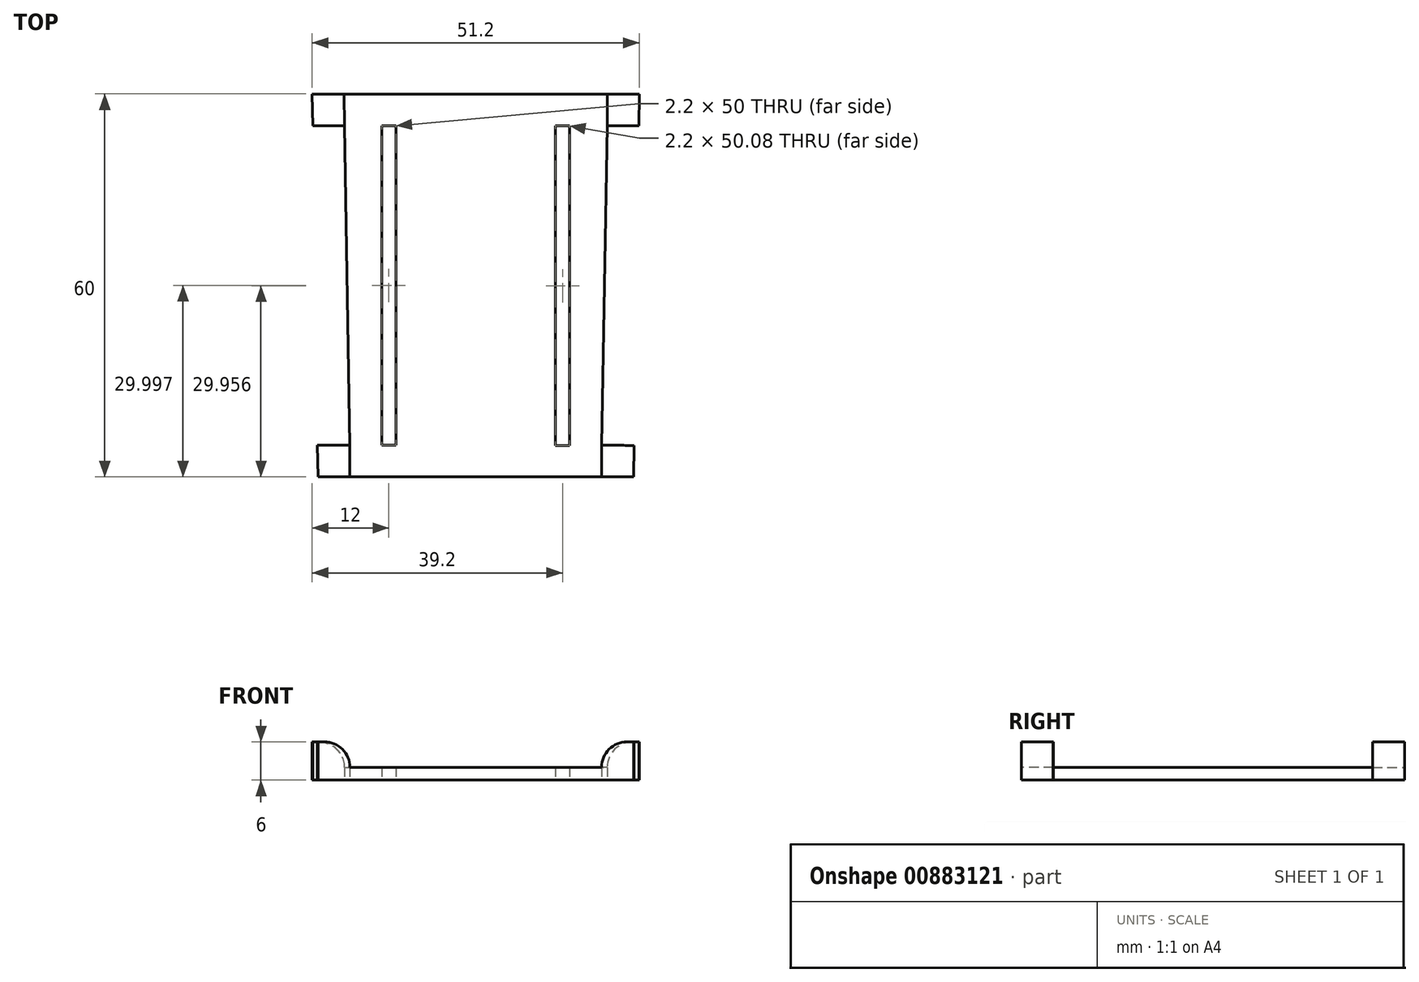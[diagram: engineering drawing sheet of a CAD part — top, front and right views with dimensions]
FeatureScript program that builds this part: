
annotation { "Feature Type Name" : "Feature", "Feature Type Description" : "" }
export const myFeature = defineFeature(function(context is Context, id is Id, definition is map)
    precondition{}
    {
        {
            var Q0;
            Q0=qCreatedBy(makeId("Top.planeOp"),FACE);
            var sketch = newSketch(context, id + "F0", { "sketchPlane" : qUnion([Q0])});
            skLineSegment(sketch, "E0", {"start": v(3.97, -2.01) * mm, "end": v(3.07, 57.99) * mm});
            skLineSegment(sketch, "E1", {"start": v(3.07, 57.99) * mm, "end": v(54.27, 57.99) * mm});
            skLineSegment(sketch, "E2", {"start": v(54.27, 57.99) * mm, "end": v(53.37, -2.01) * mm});
            skLineSegment(sketch, "E3", {"start": v(53.37, -2.01) * mm, "end": v(3.97, -2.01) * mm});
            skLineSegment(sketch, "E4", {"start": v(28.67, 57.99) * mm, "end": v(28.67, -2.01) * mm, "construction": true});
            skLineSegment(sketch, "E5.bottom", {"start": v(41.17, 2.99) * mm, "end": v(16.17, 2.99) * mm});
            skLineSegment(sketch, "E5.top", {"start": v(41.17, 52.99) * mm, "end": v(16.17, 52.99) * mm});
            skLineSegment(sketch, "E5.left", {"start": v(41.17, 2.99) * mm, "end": v(41.17, 52.99) * mm});
            skLineSegment(sketch, "E5.right", {"start": v(16.17, 2.99) * mm, "end": v(16.17, 52.99) * mm});
            skPoint(sketch, "E5.middle", {"position": v(28.67, 27.99) * mm});
            skLineSegment(sketch, "E6", {"start": v(3.97, -2.01) * mm, "end": v(8.97, -2.01) * mm});
            skLineSegment(sketch, "E7", {"start": v(3.07, 57.99) * mm, "end": v(8.07, 57.99) * mm});
            skLineSegment(sketch, "E8", {"start": v(8.97, -2.01) * mm, "end": v(3.97, -2.01) * mm});
            skLineSegment(sketch, "E9", {"start": v(54.27, 57.99) * mm, "end": v(49.27, 57.99) * mm});
            skLineSegment(sketch, "E10", {"start": v(53.37, -2.01) * mm, "end": v(48.37, -2.01) * mm});
            skLineSegment(sketch, "E11", {"start": v(8.07, 57.99) * mm, "end": v(8.15, 52.99) * mm});
            skPoint(sketch, "E11.endSnap0", {"position": v(28.67, 52.99) * mm});
            skLineSegment(sketch, "E12", {"start": v(8.15, 52.99) * mm, "end": v(3.15, 52.99) * mm});
            skLineSegment(sketch, "E13", {"start": v(49.27, 57.99) * mm, "end": v(49.27, 52.99) * mm});
            skLineSegment(sketch, "E14", {"start": v(49.27, 52.99) * mm, "end": v(54.2, 52.99) * mm});
            skLineSegment(sketch, "E15", {"start": v(8.97, -2.01) * mm, "end": v(8.97, 2.99) * mm});
            skLineSegment(sketch, "E16", {"start": v(8.97, 2.99) * mm, "end": v(3.9, 2.99) * mm});
            skLineSegment(sketch, "E17", {"start": v(48.37, -2.01) * mm, "end": v(48.37, 2.99) * mm});
            skLineSegment(sketch, "E18", {"start": v(48.37, 2.99) * mm, "end": v(53.44, 2.91) * mm});
            skLineSegment(sketch, "E19.bottom", {"start": v(41.17, 52.99) * mm, "end": v(43.37, 52.99) * mm});
            skLineSegment(sketch, "E19.top", {"start": v(41.17, 2.9) * mm, "end": v(43.37, 2.9) * mm});
            skLineSegment(sketch, "E19.left", {"start": v(41.17, 52.99) * mm, "end": v(41.17, 2.9) * mm});
            skLineSegment(sketch, "E19.right", {"start": v(43.37, 52.99) * mm, "end": v(43.37, 2.9) * mm});
            skLineSegment(sketch, "E20.bottom", {"start": v(16.17, 52.99) * mm, "end": v(13.97, 52.99) * mm});
            skLineSegment(sketch, "E20.top", {"start": v(16.17, 2.99) * mm, "end": v(13.97, 2.99) * mm});
            skLineSegment(sketch, "E20.left", {"start": v(16.17, 52.99) * mm, "end": v(16.17, 2.99) * mm});
            skLineSegment(sketch, "E20.right", {"start": v(13.97, 52.99) * mm, "end": v(13.97, 2.99) * mm});
            skLineSegment(sketch, "E21", {"start": v(49.27, 52.99) * mm, "end": v(48.37, 2.99) * mm});
            skLineSegment(sketch, "E22", {"start": v(8.15, 52.99) * mm, "end": v(8.97, 2.99) * mm});
            skSolve(sketch);
        }
        {
            var Q0;
            Q0=makeQuery(id+"F0.imprint","IMPRINT",FACE,{"disambiguationData":[TD([[makeQuery(id+"F0.imprint","IMPRINT",EDGE,{"derivedFrom":sQuery(id+"F0.wireOp",EDGE,"E5.bottom")}),1.0]])]});
            var Q1;
            {var subQ3=sQuery(id+"F0.wireOp",EDGE,"E13");Q1=makeQuery(id+"F0.imprint","IMPRINT",FACE,{"disambiguationData":[TD([[makeQuery(id+"F0.imprint","IMPRINT",EDGE,{"derivedFrom":subQ3}),1.0]])]});}
            var Q2;
            {var subQ4=sQuery(id+"F0.wireOp",EDGE,"E11");Q2=makeQuery(id+"F0.imprint","IMPRINT",FACE,{"disambiguationData":[TD([[makeQuery(id+"F0.imprint","IMPRINT",EDGE,{"derivedFrom":subQ4}),-1.0]])]});}
            var Q3;
            {var subQ4=sQuery(id+"F0.wireOp",EDGE,"E15");Q3=makeQuery(id+"F0.imprint","IMPRINT",FACE,{"disambiguationData":[TD([[makeQuery(id+"F0.imprint","IMPRINT",EDGE,{"derivedFrom":subQ4}),1.0]])]});}
            var Q4;
            {var subQ4=sQuery(id+"F0.wireOp",EDGE,"E17");Q4=makeQuery(id+"F0.imprint","IMPRINT",FACE,{"disambiguationData":[TD([[makeQuery(id+"F0.imprint","IMPRINT",EDGE,{"derivedFrom":subQ4}),-1.0]])]});}
            var Q5;
            Q5=makeQuery(id+"F0.imprint","IMPRINT",FACE,{"disambiguationData":[TD([[makeQuery(id+"F0.imprint","IMPRINT",EDGE,{"derivedFrom":sQuery(id+"F0.wireOp",EDGE,"E5.bottom")}),-1.0]])]});
            extrude(context, id + "F1", {"entities" : qUnion([Q0, Q1, Q2, Q3, Q4, Q5]), "depth" : 2 * mm, "offsetDistance" : 25 * mm});
        }
        {
            var Q0;
            {var subQ4=sQuery(id+"F0.wireOp",EDGE,"E15");Q0=makeQuery(id+"F0.imprint","IMPRINT",FACE,{"disambiguationData":[TD([[makeQuery(id+"F0.imprint","IMPRINT",EDGE,{"derivedFrom":subQ4}),1.0]])]});}
            var Q1;
            {var subQ4=sQuery(id+"F0.wireOp",EDGE,"E17");Q1=makeQuery(id+"F0.imprint","IMPRINT",FACE,{"disambiguationData":[TD([[makeQuery(id+"F0.imprint","IMPRINT",EDGE,{"derivedFrom":subQ4}),-1.0]])]});}
            var Q2;
            {var subQ3=sQuery(id+"F0.wireOp",EDGE,"E13");Q2=makeQuery(id+"F0.imprint","IMPRINT",FACE,{"disambiguationData":[TD([[makeQuery(id+"F0.imprint","IMPRINT",EDGE,{"derivedFrom":subQ3}),1.0]])]});}
            var Q3;
            {var subQ4=sQuery(id+"F0.wireOp",EDGE,"E11");Q3=makeQuery(id+"F0.imprint","IMPRINT",FACE,{"disambiguationData":[TD([[makeQuery(id+"F0.imprint","IMPRINT",EDGE,{"derivedFrom":subQ4}),-1.0]])]});}
            extrude(context, id + "F2", {"entities" : qUnion([Q0, Q1, Q2, Q3]), "operationType" : NewBodyOperationType.ADD, "depth" : 6 * mm, "offsetDistance" : 25 * mm});
        }
        {
            var Q0;
            Q0=makeQuery(id+"F2.opExtrude","CAP_EDGE",EDGE,{"disambiguationData":[OSD([sQuery(id+"F0.wireOp",EDGE,"E15")])],"isStart":false});
            var Q1;
            Q1=makeQuery(id+"F2.opExtrude","CAP_EDGE",EDGE,{"disambiguationData":[OSD([sQuery(id+"F0.wireOp",EDGE,"E11")])],"isStart":false});
            var Q2;
            Q2=makeQuery(id+"F2.opExtrude","CAP_EDGE",EDGE,{"disambiguationData":[OSD([sQuery(id+"F0.wireOp",EDGE,"E13")])],"isStart":false});
            var Q3;
            Q3=makeQuery(id+"F2.opExtrude","CAP_EDGE",EDGE,{"disambiguationData":[OSD([sQuery(id+"F0.wireOp",EDGE,"E17")])],"isStart":false});
            fillet(context, id + "F3", {"entities" : qUnion([Q0, Q1, Q2, Q3]), "radius" : 4 * mm, "tangentPropagation" : true, "allowEdgeOverflow" : false});
        }
    });
